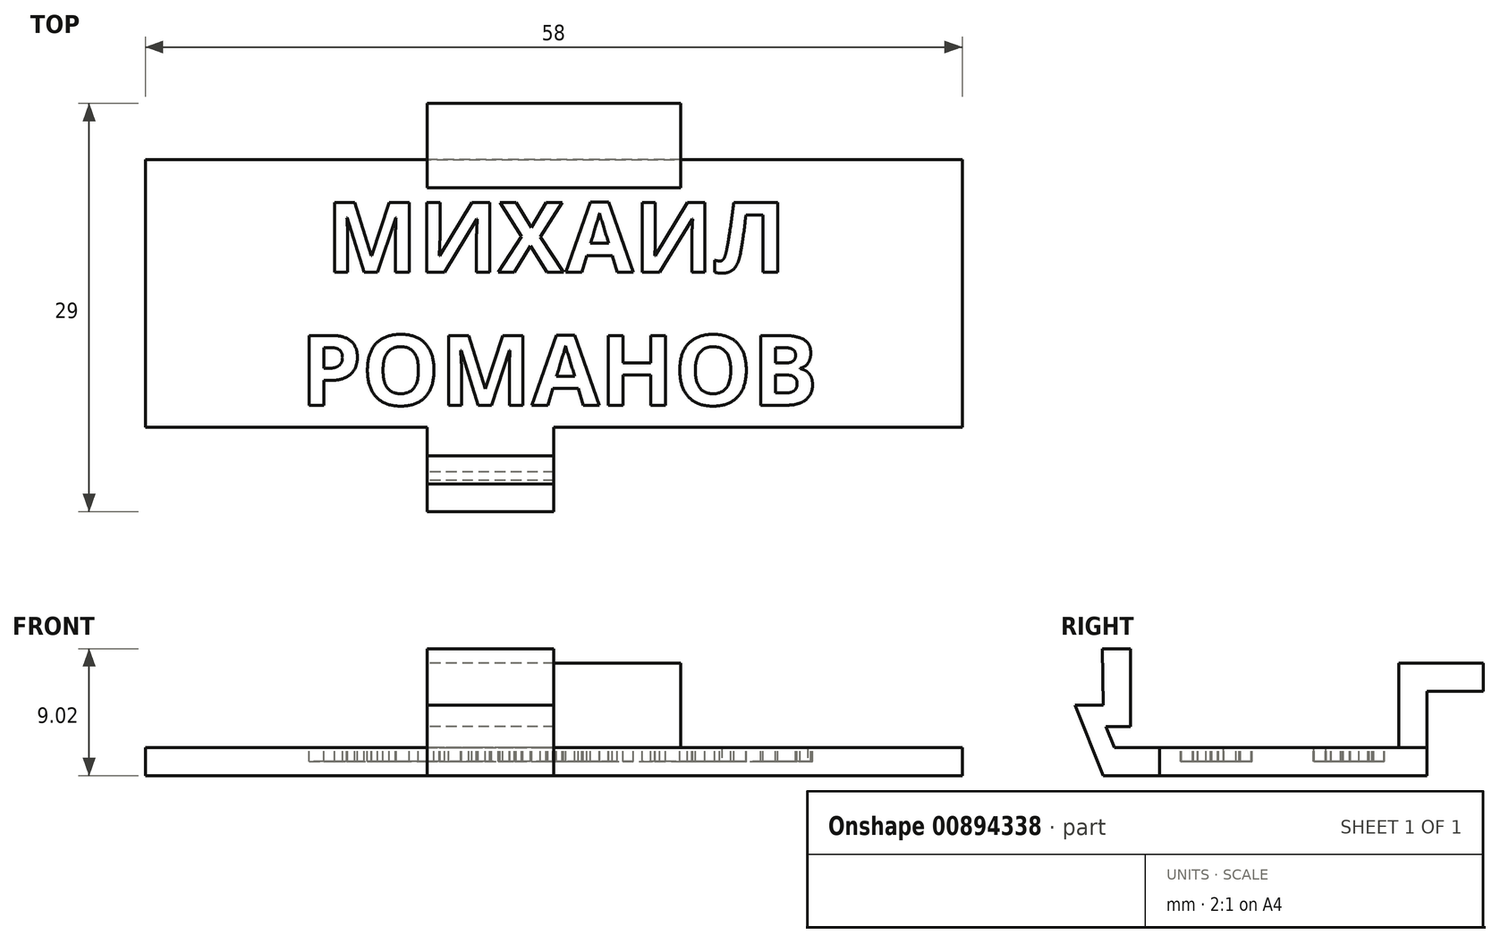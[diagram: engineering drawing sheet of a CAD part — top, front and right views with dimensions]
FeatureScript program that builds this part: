
annotation { "Feature Type Name" : "Feature", "Feature Type Description" : "" }
export const myFeature = defineFeature(function(context is Context, id is Id, definition is map)
    precondition{}
    {
        {
            var Q0;
            Q0=qCreatedBy(makeId("Top.planeOp"),FACE);
            var sketch = newSketch(context, id + "F0", { "sketchPlane" : qUnion([Q0])});
            skLineSegment(sketch, "E0.bottom", {"start": v(0, 19) * mm, "end": v(58, 19) * mm});
            skLineSegment(sketch, "E0.top", {"start": v(0, 0) * mm, "end": v(58, 0) * mm});
            skLineSegment(sketch, "E0.left", {"start": v(0, 19) * mm, "end": v(0, 0) * mm});
            skLineSegment(sketch, "E0.right", {"start": v(58, 19) * mm, "end": v(58, 0) * mm});
            skSolve(sketch);
        }
        {
            var Q0;
            Q0 = qSketchRegion(id + "F0", true);
            extrude(context, id + "F1", {"entities" : qUnion([Q0]), "depth" : 2 * mm, "offsetDistance" : 25 * mm});
        }
        {
            var Q0;
            Q0=makeQuery(id+"F1.opExtrude","SWEPT_FACE",FACE,{"disambiguationData":[OSD([sQuery(id+"F0.wireOp",EDGE,"E0.left")])]});
            cPlane(context, id + "F2", {"entities" : qUnion([Q0]), "cplaneType" : CPlaneType.OFFSET, "offset" : 20 * mm, "oppositeDirection" : true, "width" : 150 * mm, "height" : 150 * mm});
        }
        {
            var Q0;
            Q0=qCreatedBy(id+"F2.planeOp",FACE);
            var sketch = newSketch(context, id + "F3", { "sketchPlane" : qUnion([Q0])});
            skLineSegment(sketch, "E1", {"start": v(0, 0) * mm, "end": v(4, 0) * mm});
            skLineSegment(sketch, "E2", {"start": v(4, 0) * mm, "end": v(6, 5) * mm});
            skLineSegment(sketch, "E3", {"start": v(6, 5) * mm, "end": v(4, 5) * mm});
            skLineSegment(sketch, "E4", {"start": v(4, 5) * mm, "end": v(4.04, 9) * mm});
            skLineSegment(sketch, "E5", {"start": v(4.04, 9) * mm, "end": v(2.05, 9.02) * mm});
            skLineSegment(sketch, "E6", {"start": v(2.05, 9.02) * mm, "end": v(2.05, 3.5) * mm});
            skLineSegment(sketch, "E7", {"start": v(2.05, 3.5) * mm, "end": v(3.78, 3.5) * mm});
            skLineSegment(sketch, "E8", {"start": v(3.78, 3.5) * mm, "end": v(3.18, 2) * mm});
            skLineSegment(sketch, "E9", {"start": v(3.18, 2) * mm, "end": v(0, 2) * mm});
            skLineSegment(sketch, "E10", {"start": v(0, 2) * mm, "end": v(0, 0) * mm});
            skLineSegment(sketch, "E11", {"start": v(-19, 2) * mm, "end": v(-19, 6) * mm});
            skLineSegment(sketch, "E12", {"start": v(-19, 6) * mm, "end": v(-23, 6) * mm});
            skLineSegment(sketch, "E13", {"start": v(-23, 6) * mm, "end": v(-23, 8) * mm});
            skLineSegment(sketch, "E14", {"start": v(-23, 8) * mm, "end": v(-17, 8) * mm});
            skLineSegment(sketch, "E15", {"start": v(-17, 8) * mm, "end": v(-17, 2) * mm});
            skLineSegment(sketch, "E16", {"start": v(-17, 2) * mm, "end": v(-19, 2) * mm});
            skSolve(sketch);
        }
        {
            var Q0;
            Q0=makeQuery(id+"F3.imprint","IMPRINT",FACE,{"disambiguationData":[TD([[makeQuery(id+"F3.imprint","IMPRINT",EDGE,{"derivedFrom":sQuery(id+"F3.wireOp",EDGE,"E1")}),1.0]])]});
            extrude(context, id + "F4", {"entities" : qUnion([Q0]), "operationType" : NewBodyOperationType.ADD, "oppositeDirection" : true, "depth" : 9 * mm, "offsetDistance" : 25 * mm});
        }
        {
            var Q0;
            Q0=makeQuery(id+"F3.imprint","IMPRINT",FACE,{"disambiguationData":[TD([[makeQuery(id+"F3.imprint","IMPRINT",EDGE,{"derivedFrom":sQuery(id+"F3.wireOp",EDGE,"E11")}),-1.0]])]});
            extrude(context, id + "F5", {"entities" : qUnion([Q0]), "operationType" : NewBodyOperationType.ADD, "oppositeDirection" : true, "depth" : 18 * mm, "offsetDistance" : 25 * mm});
        }
        {
            var Q0;
            Q0=makeQuery(id+"F4.boolean.opBoolean","MERGE",FACE,{"derivedFrom":[makeQuery(id+"F1.opExtrude","CAP_FACE",FACE,{"disambiguationData":[OSD([sQuery(id+"F0.wireOp",EDGE,"E0.bottom"),sQuery(id+"F0.wireOp",EDGE,"E0.top"),sQuery(id+"F0.wireOp",EDGE,"E0.left"),sQuery(id+"F0.wireOp",EDGE,"E0.right")])],"isStart":false}),makeQuery(id+"F4.opExtrude","SWEPT_FACE",FACE,{"disambiguationData":[OSD([sQuery(id+"F3.wireOp",EDGE,"E9")])]})]});
            cPlane(context, id + "F6", {"entities" : qUnion([Q0]), "cplaneType" : CPlaneType.OFFSET, "offset" : 0 * mm, "oppositeDirection" : true, "width" : 150 * mm, "height" : 150 * mm});
        }
        {
            var Q0;
            Q0=qCreatedBy(id+"F6.planeOp",FACE);
            var sketch = newSketch(context, id + "F7", { "sketchPlane" : qUnion([Q0])});
            skText(sketch, "E17", { "text": " МИХАИЛ\nРОМАНОВ", "fontName": "OpenSans-Bold.ttf"});
            const initialGuessF7  = {"E17": [0.011, 0.011, 1, 0, 0.005]};
            skSetInitialGuess(sketch, initialGuessF7);
            skSolve(sketch);
        }
        {
            var Q0;
            Q0 = qSketchRegion(id + "F7", true);
            extrude(context, id + "F8", {"entities" : qUnion([Q0]), "operationType" : NewBodyOperationType.REMOVE, "oppositeDirection" : true, "depth" : 1 * mm, "offsetDistance" : 25 * mm});
        }
    });
